# Revit family: 712-0120-001-DN65
name_source: partatom
category: Pipe Fittings
units: mm (PartAtom-declared; Revit-internal decimal feet)

## family parameters
Always vertical = Yes
Cut with Voids When Loaded = No
Part Type = Elbow
Round Connector Dimension = Use Diameter
Shared = No
Work Plane-Based = No

## types (1)
- DN065_PN10/16
    A = 11.25°
    Body_wallthickness = 80 mm  [stored 0.262467 ft]
    DN 65_PN10/16 = 712-0065-01-201
    DN065_PN10/16 = Yes
    Description_ = AVK FLANGED BEND 11.25° W/LOOSE FLANGES, PN 10/16
    FOD = 93 mm
    Flange_thickness = 17 mm  [stored 0.0557743 ft]
    ID(Radius) = 33 mm
    L = 119 mm  [stored 0.39042 ft]
    L_Ref = 60 mm  [stored 0.19685 ft]
    Nominal Diameter(DN) = 65 mm  [stored 0.213255 ft]
    URL product pages = https://www.avkvalves.com

note: [stored X ft] marks values corroborated as IEEE doubles in the binary element streams (Revit-internal decimal feet)

## geometry (parser evidence)
native form markers: Sweep x17
no freeform markers — native parametric forms only
